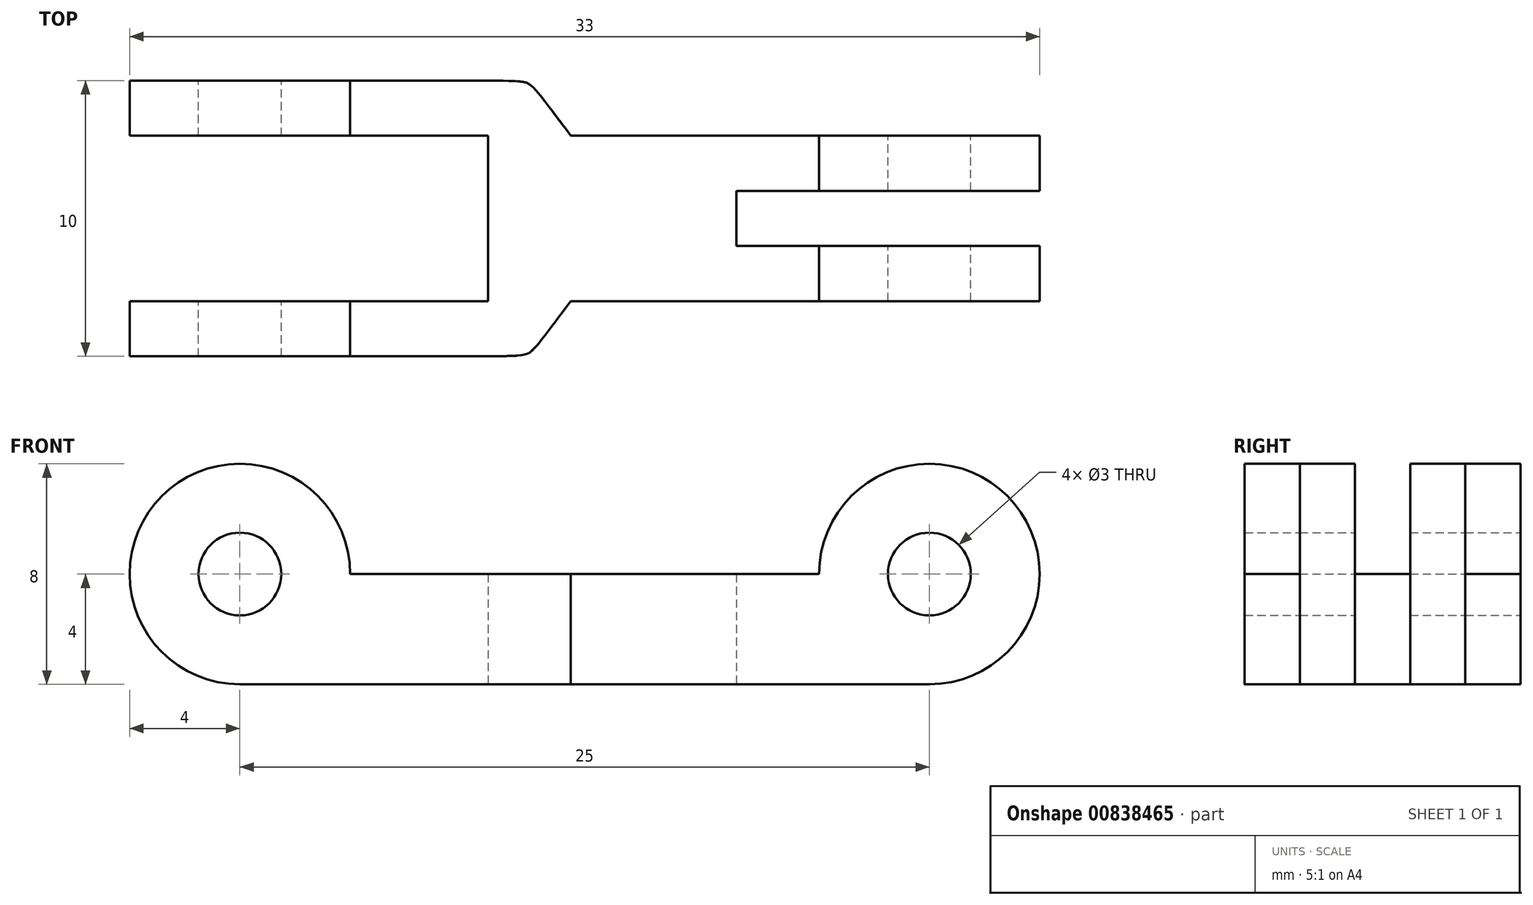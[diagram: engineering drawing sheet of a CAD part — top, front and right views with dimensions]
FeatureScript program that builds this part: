
annotation { "Feature Type Name" : "Feature", "Feature Type Description" : "" }
export const myFeature = defineFeature(function(context is Context, id is Id, definition is map)
    precondition{}
    {
        {
            var Q0;
            Q0=qCreatedBy(makeId("Front.planeOp"),FACE);
            var sketch = newSketch(context, id + "F0", { "sketchPlane" : qUnion([Q0])});
            skLineSegment(sketch, "E0.bottom", {"start": v(12.5, 2) * mm, "end": v(-12.5, 2) * mm});
            skLineSegment(sketch, "E0.top", {"start": v(12.5, -2) * mm, "end": v(-12.5, -2) * mm});
            skLineSegment(sketch, "E0.left", {"start": v(12.5, 2) * mm, "end": v(12.5, -2) * mm});
            skLineSegment(sketch, "E0.right", {"start": v(-12.5, 2) * mm, "end": v(-12.5, -2) * mm});
            skPoint(sketch, "E0.middle", {"position": v(0, 0) * mm});
            skLineSegment(sketch, "E1", {"start": v(-3.5, 2) * mm, "end": v(-3.5, -2) * mm});
            skLineSegment(sketch, "E2", {"start": v(-0.5, 2) * mm, "end": v(-0.5, -2) * mm});
            skCircle(sketch, "E3", {"center": v(12.5, 2) * mm, "radius": 4 * mm});
            skCircle(sketch, "E4", {"center": v(-12.5, 2) * mm, "radius": 4 * mm});
            skCircle(sketch, "E5", {"center": v(12.5, 2) * mm, "radius": 1.5 * mm});
            skCircle(sketch, "E6", {"center": v(-12.5, 2) * mm, "radius": 1.5 * mm});
            skLineSegment(sketch, "E7", {"start": v(5.5, 2) * mm, "end": v(5.5, -2) * mm});
            skSolve(sketch);
        }
        {
            var Q0;
            {var subQ0=sQuery(id+"F0.wireOp",EDGE,"E4");var subQ1=sQuery(id+"F0.wireOp",EDGE,"E0.bottom");var subQ2=makeQuery(id+"F0.imprint","INTERSECT",VERTEX,{"derivedFrom":[subQ1,subQ0]});Q0=makeQuery(id+"F0.imprint","IMPRINT",FACE,{"disambiguationData":[TD([[makeQuery(id+"F0.imprint","IMPRINT",EDGE,{"disambiguationData":[TD([[subQ2,-1.0]])],"derivedFrom":subQ1}),-1.0]])]});}
            var Q1;
            {var subQ0=sQuery(id+"F0.wireOp",EDGE,"E4");var subQ1=sQuery(id+"F0.wireOp",EDGE,"E0.bottom");var subQ2=makeQuery(id+"F0.imprint","INTERSECT",VERTEX,{"derivedFrom":[subQ1,subQ0]});Q1=makeQuery(id+"F0.imprint","IMPRINT",FACE,{"disambiguationData":[TD([[makeQuery(id+"F0.imprint","IMPRINT",EDGE,{"disambiguationData":[TD([[subQ2,-1.0]])],"derivedFrom":subQ1}),1.0]])]});}
            var Q2;
            {var subQ0=sQuery(id+"F0.wireOp",EDGE,"E1");Q2=makeQuery(id+"F0.imprint","IMPRINT",FACE,{"disambiguationData":[TD([[makeQuery(id+"F0.imprint","IMPRINT",EDGE,{"derivedFrom":subQ0}),-1.0]])]});}
            var Q3;
            {var subQ0=sQuery(id+"F0.wireOp",EDGE,"E1");Q3=makeQuery(id+"F0.imprint","IMPRINT",FACE,{"disambiguationData":[TD([[makeQuery(id+"F0.imprint","IMPRINT",EDGE,{"derivedFrom":subQ0}),1.0]])]});}
            extrude(context, id + "F1", {"entities" : qUnion([Q0, Q1, Q2, Q3]), "depth" : 10 * mm, "offsetDistance" : 25 * mm, "symmetric" : true});
        }
        {
            var Q0;
            {var subQ0=sQuery(id+"F0.wireOp",EDGE,"E2");Q0=makeQuery(id+"F0.imprint","IMPRINT",FACE,{"disambiguationData":[TD([[makeQuery(id+"F0.imprint","IMPRINT",EDGE,{"derivedFrom":subQ0}),1.0]])]});}
            var Q1;
            {var subQ0=sQuery(id+"F0.wireOp",EDGE,"E7");Q1=makeQuery(id+"F0.imprint","IMPRINT",FACE,{"disambiguationData":[TD([[makeQuery(id+"F0.imprint","IMPRINT",EDGE,{"derivedFrom":subQ0}),1.0]])]});}
            var Q2;
            {var subQ0=sQuery(id+"F0.wireOp",EDGE,"E3");var subQ1=sQuery(id+"F0.wireOp",EDGE,"E0.bottom");var subQ2=makeQuery(id+"F0.imprint","INTERSECT",VERTEX,{"derivedFrom":[subQ1,subQ0]});Q2=makeQuery(id+"F0.imprint","IMPRINT",FACE,{"disambiguationData":[TD([[makeQuery(id+"F0.imprint","IMPRINT",EDGE,{"disambiguationData":[TD([[subQ2,1.0]])],"derivedFrom":subQ1}),1.0]])]});}
            var Q3;
            {var subQ0=sQuery(id+"F0.wireOp",EDGE,"E3");var subQ1=sQuery(id+"F0.wireOp",EDGE,"E0.bottom");var subQ2=makeQuery(id+"F0.imprint","INTERSECT",VERTEX,{"derivedFrom":[subQ1,subQ0]});Q3=makeQuery(id+"F0.imprint","IMPRINT",FACE,{"disambiguationData":[TD([[makeQuery(id+"F0.imprint","IMPRINT",EDGE,{"disambiguationData":[TD([[subQ2,1.0]])],"derivedFrom":subQ1}),-1.0]])]});}
            extrude(context, id + "F2", {"entities" : qUnion([Q0, Q1, Q2, Q3]), "operationType" : NewBodyOperationType.ADD, "depth" : 6 * mm, "offsetDistance" : 25 * mm, "symmetric" : true});
        }
        {
            var Q0;
            {var subQ0=sQuery(id+"F0.wireOp",EDGE,"E1");Q0=makeQuery(id+"F0.imprint","IMPRINT",FACE,{"disambiguationData":[TD([[makeQuery(id+"F0.imprint","IMPRINT",EDGE,{"derivedFrom":subQ0}),-1.0]])]});}
            var Q1;
            {var subQ0=sQuery(id+"F0.wireOp",EDGE,"E4");var subQ1=sQuery(id+"F0.wireOp",EDGE,"E0.bottom");var subQ2=makeQuery(id+"F0.imprint","INTERSECT",VERTEX,{"derivedFrom":[subQ1,subQ0]});Q1=makeQuery(id+"F0.imprint","IMPRINT",FACE,{"disambiguationData":[TD([[makeQuery(id+"F0.imprint","IMPRINT",EDGE,{"disambiguationData":[TD([[subQ2,-1.0]])],"derivedFrom":subQ1}),1.0]])]});}
            var Q2;
            {var subQ0=sQuery(id+"F0.wireOp",EDGE,"E4");var subQ1=sQuery(id+"F0.wireOp",EDGE,"E0.bottom");var subQ2=makeQuery(id+"F0.imprint","INTERSECT",VERTEX,{"derivedFrom":[subQ1,subQ0]});Q2=makeQuery(id+"F0.imprint","IMPRINT",FACE,{"disambiguationData":[TD([[makeQuery(id+"F0.imprint","IMPRINT",EDGE,{"disambiguationData":[TD([[subQ2,-1.0]])],"derivedFrom":subQ1}),-1.0]])]});}
            extrude(context, id + "F3", {"entities" : qUnion([Q0, Q1, Q2]), "operationType" : NewBodyOperationType.REMOVE, "depth" : 6 * mm, "offsetDistance" : 25 * mm, "symmetric" : true});
        }
        {
            var Q0;
            {var subQ0=sQuery(id+"F0.wireOp",EDGE,"E7");Q0=makeQuery(id+"F0.imprint","IMPRINT",FACE,{"disambiguationData":[TD([[makeQuery(id+"F0.imprint","IMPRINT",EDGE,{"derivedFrom":subQ0}),1.0]])]});}
            var Q1;
            {var subQ0=sQuery(id+"F0.wireOp",EDGE,"E3");var subQ1=sQuery(id+"F0.wireOp",EDGE,"E0.bottom");var subQ2=makeQuery(id+"F0.imprint","INTERSECT",VERTEX,{"derivedFrom":[subQ1,subQ0]});Q1=makeQuery(id+"F0.imprint","IMPRINT",FACE,{"disambiguationData":[TD([[makeQuery(id+"F0.imprint","IMPRINT",EDGE,{"disambiguationData":[TD([[subQ2,1.0]])],"derivedFrom":subQ1}),1.0]])]});}
            var Q2;
            {var subQ0=sQuery(id+"F0.wireOp",EDGE,"E3");var subQ1=sQuery(id+"F0.wireOp",EDGE,"E0.bottom");var subQ2=makeQuery(id+"F0.imprint","INTERSECT",VERTEX,{"derivedFrom":[subQ1,subQ0]});Q2=makeQuery(id+"F0.imprint","IMPRINT",FACE,{"disambiguationData":[TD([[makeQuery(id+"F0.imprint","IMPRINT",EDGE,{"disambiguationData":[TD([[subQ2,1.0]])],"derivedFrom":subQ1}),-1.0]])]});}
            extrude(context, id + "F4", {"entities" : qUnion([Q0, Q1, Q2]), "operationType" : NewBodyOperationType.REMOVE, "oppositeDirection" : true, "depth" : 2 * mm, "offsetDistance" : 25 * mm, "symmetric" : true});
        }
        {
            var Q0;
            Q0=makeQuery(id+"F1.opExtrude","CAP_EDGE",EDGE,{"disambiguationData":[OSD([sQuery(id+"F0.wireOp",EDGE,"E2")])],"isStart":false});
            var Q1;
            Q1=makeQuery(id+"F1.opExtrude","CAP_EDGE",EDGE,{"disambiguationData":[OSD([sQuery(id+"F0.wireOp",EDGE,"E2")])],"isStart":true});
            fillet(context, id + "F5", {"entities" : qUnion([Q0, Q1]), "radius" : 5 * mm, "tangentPropagation" : true, "rho" : 0.9, "crossSection" : FilletCrossSection.CONIC, "allowEdgeOverflow" : false});
        }
    });
